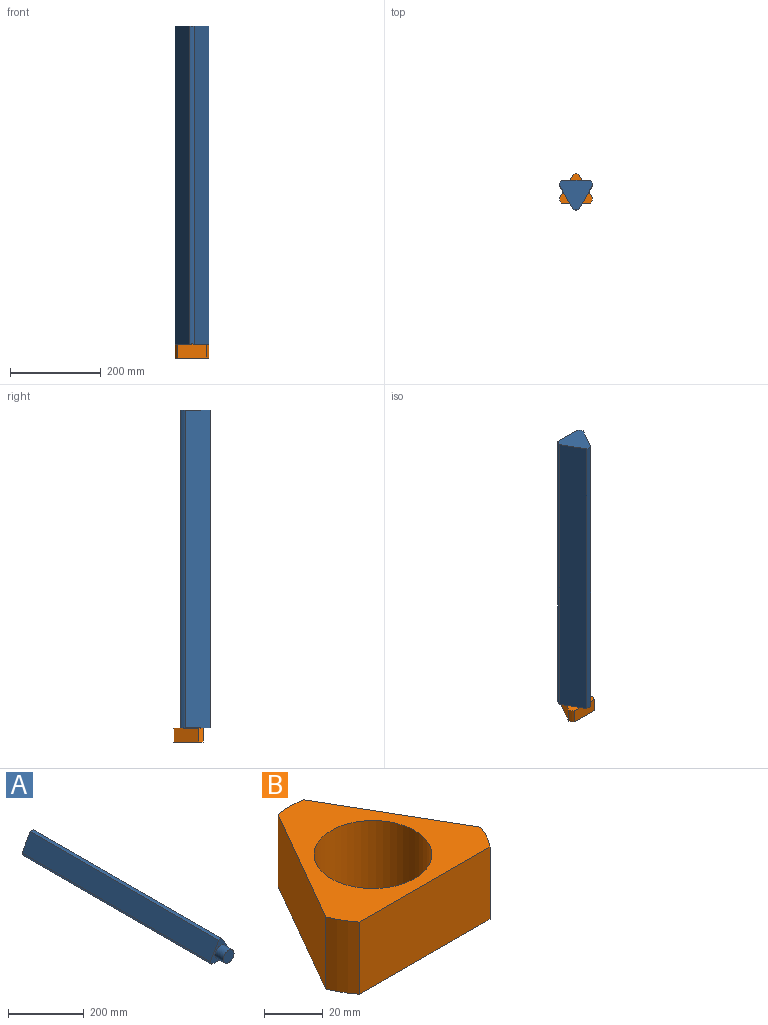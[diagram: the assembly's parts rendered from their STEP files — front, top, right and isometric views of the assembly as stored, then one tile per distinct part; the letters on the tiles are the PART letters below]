
ASSEMBLY  parts=2 mates=1
PART A: 10 faces, bbox 74.5x733x65 mm
  f0: cylinder r=40mm len=702mm, axis (0,1,0), area 8510.1mm2, adj f1,f5,f6,f7
  f1: plane 702x54.08mm, normal (-0.87,0,0.5), area 43839.9mm2, adj f0,f2,f6,f7
  f2: cylinder r=40mm len=702mm, axis (0,1,0), area 8510.1mm2, adj f1,f3,f6,f7
  f3: plane 702x62.45mm, normal (0,0,-1), area 43839.9mm2, adj f2,f4,f6,f7
  f4: cylinder r=40mm len=702mm, axis (0,1,0), area 8510.1mm2, adj f3,f5,f6,f7
  f5: plane 702x54.08mm, normal (0.87,0,0.5), area 43839.9mm2, adj f0,f4,f6,f7
  f6: plane 74.53x65mm, normal (0,-1,0), area 1812.6mm2, adj f0,f1,f2,f3,f4,f5,f8
  f7: plane 74.53x65mm, normal (0,1,0), area 3069.2mm2, adj f0,f1,f2,f3,f4,f5
  f8: cylinder r=20mm len=40mm, axis (0,1,0), area 3895.6mm2, adj f6,f9
  f9: plane 40x40mm, normal (0,-1,0), area 1256.6mm2, adj f8
PART B: 9 faces, bbox 74.5x65x30 mm
  f0: cylinder r=40mm len=30mm, axis (0,0,-1), area 363.7mm2, adj f1,f5,f6,f7
  f1: plane 54.08x31.23mm, normal (-0.87,0.5,0), area 1873.5mm2, adj f0,f2,f6,f7
  f2: cylinder r=40mm len=30mm, axis (0,0,-1), area 363.7mm2, adj f1,f3,f6,f7
  f3: plane 62.45x30mm, normal (0,-1,0), area 1873.5mm2, adj f2,f4,f6,f7
  f4: cylinder r=40mm len=30mm, axis (0,0,-1), area 363.7mm2, adj f3,f5,f6,f7
  f5: plane 54.08x31.23mm, normal (0.87,0.5,0), area 1873.5mm2, adj f0,f4,f6,f7
  f6: plane 74.53x65mm, normal (0,0,1), area 1812.6mm2, adj f0,f1,f2,f3,f4,f5,f8
  f7: plane 74.53x65mm, normal (0,0,-1), area 1812.6mm2, adj f0,f1,f2,f3,f4,f5,f8
  f8: cylinder r=20mm len=40mm, axis (0,0,1), area 3769.9mm2, adj f6,f7
PLACE A rot(axis=(0.38,0.65,0.65),138.6deg) t=(-57.15,38.85,682)mm
PLACE B rot(axis=(0,0,1),0deg) t=(-57.15,38.85,-51)mm
MATE cylindrical B.f8 <-> A.f8  axis (0,0,-1) through (-57.15,38.85,-51)mm
